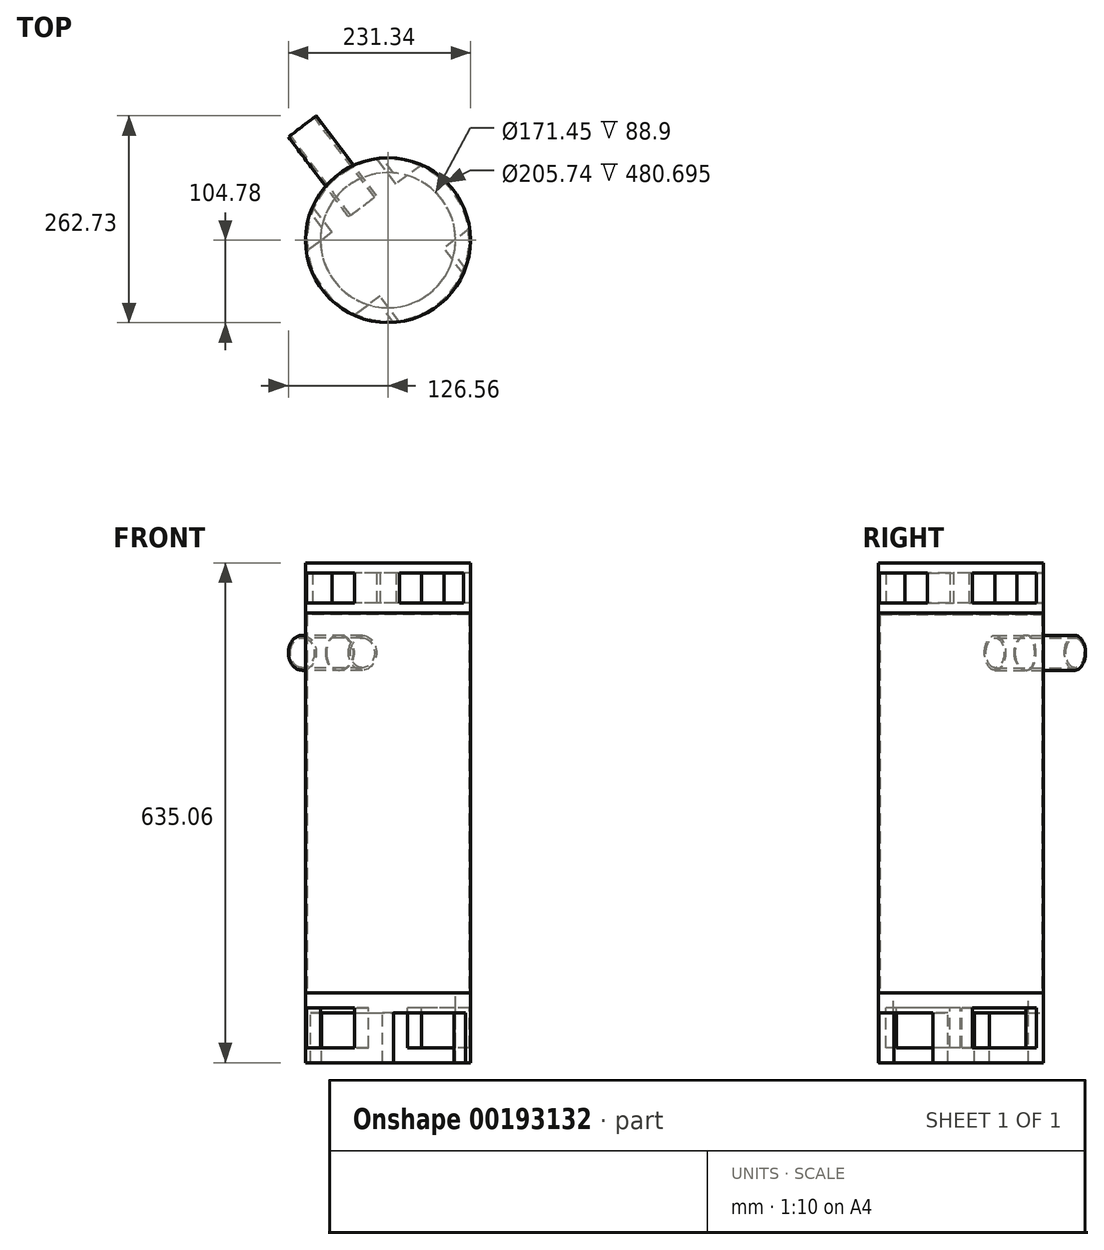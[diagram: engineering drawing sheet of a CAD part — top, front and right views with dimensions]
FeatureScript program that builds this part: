
annotation { "Feature Type Name" : "Feature", "Feature Type Description" : "" }
export const myFeature = defineFeature(function(context is Context, id is Id, definition is map)
    precondition{}
    {
        {
            var Q0;
            Q0=qCreatedBy(makeId("Top.planeOp"),FACE);
            var sketch = newSketch(context, id + "F0", { "sketchPlane" : qUnion([Q0])});
            skCircle(sketch, "E0", {"center": v(0, 0) * mm, "radius": 104.77 * mm});
            skSolve(sketch);
        }
        {
            var Q0;
            Q0 = qSketchRegion(id + "F0", true);
            extrude(context, id + "F1", {"entities" : qUnion([Q0]), "depth" : 482.6 * mm});
        }
        {
            var Q0;
            Q0=makeQuery(id+"F1.opExtrude","CAP_FACE",FACE,{"disambiguationData":[OSD([sQuery(id+"F0.wireOp",EDGE,"E0")])],"isStart":true});
            shell(context, id + "F2", {"entities" : qUnion([Q0]), "thickness" : 1.9 * mm});
        }
        {
            var Q0;
            Q0=makeQuery(id+"F1.opExtrude","CAP_FACE",FACE,{"disambiguationData":[OSD([sQuery(id+"F0.wireOp",EDGE,"E0")])],"isStart":true});
            cPlane(context, id + "F3", {"entities" : qUnion([Q0]), "cplaneType" : CPlaneType.OFFSET, "offset" : 0.03 * mm, "width" : 152.4 * mm, "height" : 152.4 * mm});
        }
        {
            var Q0;
            Q0=qCreatedBy(id+"F3.planeOp",FACE);
            var sketch = newSketch(context, id + "F4", { "sketchPlane" : qUnion([Q0])});
            skCircle(sketch, "E1.0", {"center": v(0, 0) * mm, "radius": 104.77 * mm});
            skCircle(sketch, "E2", {"center": v(0, 0) * mm, "radius": 85.72 * mm});
            skSolve(sketch);
        }
        {
            var Q0;
            Q0 = qSketchRegion(id + "F4", true);
            extrude(context, id + "F5", {"entities" : qUnion([Q0]), "depth" : 88.9 * mm});
        }
        {
            var Q0;
            Q0=makeQuery(id+"F1.opExtrude","CAP_FACE",FACE,{"disambiguationData":[OSD([sQuery(id+"F0.wireOp",EDGE,"E0")])],"isStart":false});
            cPlane(context, id + "F6", {"entities" : qUnion([Q0]), "cplaneType" : CPlaneType.OFFSET, "offset" : 0.03 * mm, "width" : 152.4 * mm, "height" : 152.4 * mm});
        }
        {
            var Q0;
            Q0=qCreatedBy(id+"F6.planeOp",FACE);
            var sketch = newSketch(context, id + "F7", { "sketchPlane" : qUnion([Q0])});
            skCircle(sketch, "E3.0", {"center": v(0, 0) * mm, "radius": 104.77 * mm});
            skLineSegment(sketch, "E4", {"start": v(0, 0) * mm, "end": v(-89.21, 54.95) * mm, "construction": true});
            skLineSegment(sketch, "E5", {"start": v(-425.15, 244.23) * mm, "end": v(-429.64, 248.82) * mm, "construction": true});
            skSolve(sketch);
        }
        {
            var Q0;
            Q0 = qSketchRegion(id + "F7", true);
            extrude(context, id + "F8", {"entities" : qUnion([Q0]), "depth" : 63.5 * mm});
        }
        {
            var Q0;
            Q0=makeQuery(id+"F8.opExtrude","CAP_FACE",FACE,{"disambiguationData":[OSD([sQuery(id+"F7.wireOp",EDGE,"E3.0"),sQuery(id+"F7.wireOp",EDGE,"PvvvyQds-Sv6C-QQrE-GDpc-XunfeWzJxLqP")])],"isStart":true});
            var sketch = newSketch(context, id + "F9", { "sketchPlane" : qUnion([Q0])});
            skLineSegment(sketch, "E6", {"start": v(0, 0) * mm, "end": v(-63, -83.72) * mm, "construction": true});
            skLineSegment(sketch, "E7", {"start": v(0, 0) * mm, "end": v(-83.72, 63) * mm, "construction": true});
            skSolve(sketch);
        }
        {
            var Q0;
            Q0=sQuery(id+"F9.wireOp",VERTEX,"E6.end");
            var Q1;
            Q1=sQuery(id+"F9.wireOp",EDGE,"E6");
            cPlane(context, id + "F10", {"entities" : qUnion([Q0, Q1]), "cplaneType" : CPlaneType.CURVE_POINT, "offset" : 25.4 * mm, "width" : 152.4 * mm, "height" : 152.4 * mm});
        }
        {
            var Q0;
            Q0=qCreatedBy(id+"F10.planeOp",FACE);
            var sketch = newSketch(context, id + "F11", { "sketchPlane" : qUnion([Q0])});
            skCircle(sketch, "E8", {"center": v(0, 431.8) * mm, "radius": 22.23 * mm});
            skPoint(sketch, "E9.0", {"position": v(0, 482.63) * mm});
            skLineSegment(sketch, "E10", {"start": v(0, 482.63) * mm, "end": v(0, 342.38) * mm, "construction": true});
            skSolve(sketch);
        }
        {
            var Q0;
            Q0 = qSketchRegion(id + "F11", true);
            extrude(context, id + "F12", {"entities" : qUnion([Q0]), "operationType" : NewBodyOperationType.REMOVE, "oppositeDirection" : true, "depth" : 25.4 * mm});
        }
        {
            var Q0;
            Q0=sQuery(id+"F9.wireOp",EDGE,"E7");
            var Q1;
            Q1=sQuery(id+"F9.wireOp",VERTEX,"E7.end");
            cPlane(context, id + "F13", {"entities" : qUnion([Q0, Q1]), "cplaneType" : CPlaneType.CURVE_POINT, "offset" : 25.4 * mm, "width" : 152.4 * mm, "height" : 152.4 * mm});
        }
        {
            var Q0;
            Q0=qCreatedBy(id+"F13.planeOp",FACE);
            var sketch = newSketch(context, id + "F14", { "sketchPlane" : qUnion([Q0])});
            skLineSegment(sketch, "E11", {"start": v(-104.78, 482.63) * mm, "end": v(-104.78, 546.13) * mm, "construction": true});
            skLineSegment(sketch, "E12", {"start": v(104.78, 546.13) * mm, "end": v(104.78, 482.63) * mm, "construction": true});
            skLineSegment(sketch, "E13.0", {"start": v(-104.78, 482.63) * mm, "end": v(104.78, 482.63) * mm, "construction": true});
            skLineSegment(sketch, "E14.0", {"start": v(-104.78, 546.13) * mm, "end": v(104.78, 546.13) * mm, "construction": true});
            skLineSegment(sketch, "E15.bottom", {"start": v(50.8, 533.43) * mm, "end": v(-50.8, 533.43) * mm});
            skLineSegment(sketch, "E15.top", {"start": v(50.8, 495.33) * mm, "end": v(-50.8, 495.33) * mm});
            skLineSegment(sketch, "E15.left", {"start": v(50.8, 533.43) * mm, "end": v(50.8, 495.33) * mm});
            skLineSegment(sketch, "E15.right", {"start": v(-50.8, 533.43) * mm, "end": v(-50.8, 495.33) * mm});
            skLineSegment(sketch, "E16", {"start": v(104.78, -0.03) * mm, "end": v(104.78, -88.93) * mm, "construction": true});
            skLineSegment(sketch, "E17", {"start": v(-104.78, -88.93) * mm, "end": v(-104.78, -0.03) * mm, "construction": true});
            skLineSegment(sketch, "E18.0", {"start": v(104.78, -88.93) * mm, "end": v(-104.78, -88.93) * mm, "construction": true});
            skLineSegment(sketch, "E19.0", {"start": v(-104.78, 0) * mm, "end": v(104.78, 0) * mm, "construction": true});
            skLineSegment(sketch, "E20.bottom", {"start": v(50.8, -69.88) * mm, "end": v(-50.8, -69.88) * mm});
            skLineSegment(sketch, "E20.top", {"start": v(50.8, -19.08) * mm, "end": v(-50.8, -19.08) * mm});
            skLineSegment(sketch, "E20.left", {"start": v(50.8, -69.88) * mm, "end": v(50.8, -19.08) * mm});
            skLineSegment(sketch, "E20.right", {"start": v(-50.8, -69.88) * mm, "end": v(-50.8, -19.08) * mm});
            skPoint(sketch, "E21", {"position": v(0, -88.93) * mm});
            skPoint(sketch, "E22", {"position": v(0, 546.13) * mm});
            skLineSegment(sketch, "E23", {"start": v(0, 546.13) * mm, "end": v(0, -88.93) * mm, "construction": true});
            skPoint(sketch, "E24", {"position": v(0, -69.88) * mm});
            skPoint(sketch, "E25", {"position": v(0, 495.33) * mm});
            skSolve(sketch);
        }
        {
            var Q0;
            Q0=makeQuery(id+"F14.imprint","IMPRINT",FACE,{"disambiguationData":[TD([[makeQuery(id+"F14.imprint","IMPRINT",EDGE,{"derivedFrom":sQuery(id+"F14.wireOp",EDGE,"E15.bottom")}),1.0]])]});
            var Q1;
            Q1=makeQuery(id+"F14.imprint","IMPRINT",FACE,{"disambiguationData":[TD([[makeQuery(id+"F14.imprint","IMPRINT",EDGE,{"derivedFrom":sQuery(id+"F14.wireOp",EDGE,"E20.bottom")}),-1.0]])]});
            extrude(context, id + "F15", {"entities" : qUnion([Q0, Q1]), "operationType" : NewBodyOperationType.REMOVE, "endBound" : BoundingType.THROUGH_ALL, "oppositeDirection" : true, "depth" : 25.4 * mm});
        }
        {
            var Q0;
            Q0=qCreatedBy(id+"F10.planeOp",FACE);
            var sketch = newSketch(context, id + "F16", { "sketchPlane" : qUnion([Q0])});
            skLineSegment(sketch, "E26.0", {"start": v(-104.78, 482.63) * mm, "end": v(104.78, 482.63) * mm, "construction": true});
            skLineSegment(sketch, "E27.0", {"start": v(-104.78, 546.13) * mm, "end": v(104.78, 546.13) * mm, "construction": true});
            skLineSegment(sketch, "E28", {"start": v(-104.78, 482.63) * mm, "end": v(-104.78, 546.13) * mm, "construction": true});
            skLineSegment(sketch, "E29", {"start": v(104.78, 546.13) * mm, "end": v(104.78, 482.63) * mm, "construction": true});
            skLineSegment(sketch, "E30.bottom", {"start": v(50.8, 533.43) * mm, "end": v(-50.8, 533.43) * mm});
            skLineSegment(sketch, "E30.top", {"start": v(50.8, 495.33) * mm, "end": v(-50.8, 495.33) * mm});
            skLineSegment(sketch, "E30.left", {"start": v(50.8, 533.43) * mm, "end": v(50.8, 495.33) * mm});
            skLineSegment(sketch, "E30.right", {"start": v(-50.8, 533.43) * mm, "end": v(-50.8, 495.33) * mm});
            skPoint(sketch, "E31", {"position": v(0, 482.63) * mm});
            skLineSegment(sketch, "E32", {"start": v(0, 482.63) * mm, "end": v(0, 546.13) * mm, "construction": true});
            skPoint(sketch, "E33", {"position": v(0, 495.33) * mm});
            skSolve(sketch);
        }
        {
            var Q0;
            Q0 = qSketchRegion(id + "F16", true);
            extrude(context, id + "F17", {"entities" : qUnion([Q0]), "operationType" : NewBodyOperationType.REMOVE, "endBound" : BoundingType.THROUGH_ALL, "oppositeDirection" : true, "depth" : 25.4 * mm});
        }
        {
            var Q0;
            Q0=qCreatedBy(id+"F10.planeOp",FACE);
            var sketch = newSketch(context, id + "F18", { "sketchPlane" : qUnion([Q0])});
            skLineSegment(sketch, "E34", {"start": v(104.78, -0.03) * mm, "end": v(104.78, -88.93) * mm, "construction": true});
            skLineSegment(sketch, "E35", {"start": v(-104.78, -88.93) * mm, "end": v(-104.78, -0.03) * mm, "construction": true});
            skLineSegment(sketch, "E36.0", {"start": v(-104.78, 0) * mm, "end": v(104.78, 0) * mm, "construction": true});
            skPoint(sketch, "E37", {"position": v(0, -88.93) * mm});
            skLineSegment(sketch, "E38", {"start": v(0, -88.93) * mm, "end": v(0, 0) * mm, "construction": true});
            skLineSegment(sketch, "E39", {"start": v(-57.15, -88.93) * mm, "end": v(-57.15, -25.43) * mm});
            skLineSegment(sketch, "E40", {"start": v(-57.15, -25.43) * mm, "end": v(57.15, -25.43) * mm});
            skLineSegment(sketch, "E41", {"start": v(57.15, -25.43) * mm, "end": v(57.15, -88.93) * mm});
            skLineSegment(sketch, "E42", {"start": v(57.15, -88.93) * mm, "end": v(-57.15, -88.93) * mm});
            skSolve(sketch);
        }
        {
            var Q0;
            Q0 = qSketchRegion(id + "F18", true);
            extrude(context, id + "F19", {"entities" : qUnion([Q0]), "operationType" : NewBodyOperationType.REMOVE, "endBound" : BoundingType.THROUGH_ALL, "oppositeDirection" : true, "depth" : 25.4 * mm});
        }
        {
            var Q0;
            Q0=qCreatedBy(id+"F13.planeOp",FACE);
            var sketch = newSketch(context, id + "F20", { "sketchPlane" : qUnion([Q0])});
            skLineSegment(sketch, "E43", {"start": v(104.78, -0.03) * mm, "end": v(104.78, -25.43) * mm, "construction": true});
            skLineSegment(sketch, "E44", {"start": v(-104.78, -25.43) * mm, "end": v(-104.78, -0.03) * mm, "construction": true});
            skLineSegment(sketch, "E45.0", {"start": v(87.82, -88.93) * mm, "end": v(-87.82, -88.93) * mm, "construction": true});
            skLineSegment(sketch, "E46.0", {"start": v(104.78, -0.03) * mm, "end": v(-104.78, -0.03) * mm, "construction": true});
            skLineSegment(sketch, "E47.bottom", {"start": v(44.45, -25.43) * mm, "end": v(-44.45, -25.43) * mm});
            skLineSegment(sketch, "E47.top", {"start": v(44.45, -63.53) * mm, "end": v(-44.45, -63.53) * mm});
            skLineSegment(sketch, "E47.left", {"start": v(44.45, -25.43) * mm, "end": v(44.45, -63.53) * mm});
            skLineSegment(sketch, "E47.right", {"start": v(-44.45, -25.43) * mm, "end": v(-44.45, -63.53) * mm});
            skPoint(sketch, "E48", {"position": v(0, -88.93) * mm});
            skLineSegment(sketch, "E49", {"start": v(0, -88.93) * mm, "end": v(0, 0) * mm, "construction": true});
            skPoint(sketch, "E50", {"position": v(0, -63.53) * mm});
            skSolve(sketch);
        }
        {
            var Q0;
            Q0 = qSketchRegion(id + "F20", true);
            extrude(context, id + "F21", {"entities" : qUnion([Q0]), "operationType" : NewBodyOperationType.REMOVE, "endBound" : BoundingType.THROUGH_ALL, "oppositeDirection" : true, "depth" : 25.4 * mm});
        }
        {
            var Q0;
            Q0=qCreatedBy(id+"F10.planeOp",FACE);
            cPlane(context, id + "F22", {"entities" : qUnion([Q0]), "cplaneType" : CPlaneType.OFFSET, "offset" : 76.2 * mm, "width" : 152.4 * mm, "height" : 152.4 * mm});
        }
        {
            var Q0;
            Q0=qCreatedBy(id+"F22.planeOp",FACE);
            var sketch = newSketch(context, id + "F23", { "sketchPlane" : qUnion([Q0])});
            skCircle(sketch, "E51.0", {"center": v(0, 431.8) * mm, "radius": 22.23 * mm, "construction": true});
            skCircle(sketch, "E52", {"center": v(0, 431.8) * mm, "radius": 22.2 * mm});
            skCircle(sketch, "E53", {"center": v(0, 431.8) * mm, "radius": 19.02 * mm});
            skSolve(sketch);
        }
        {
            var Q0;
            Q0 = qSketchRegion(id + "F23", true);
            extrude(context, id + "F24", {"entities" : qUnion([Q0]), "oppositeDirection" : true, "depth" : 127 * mm});
        }
    });
